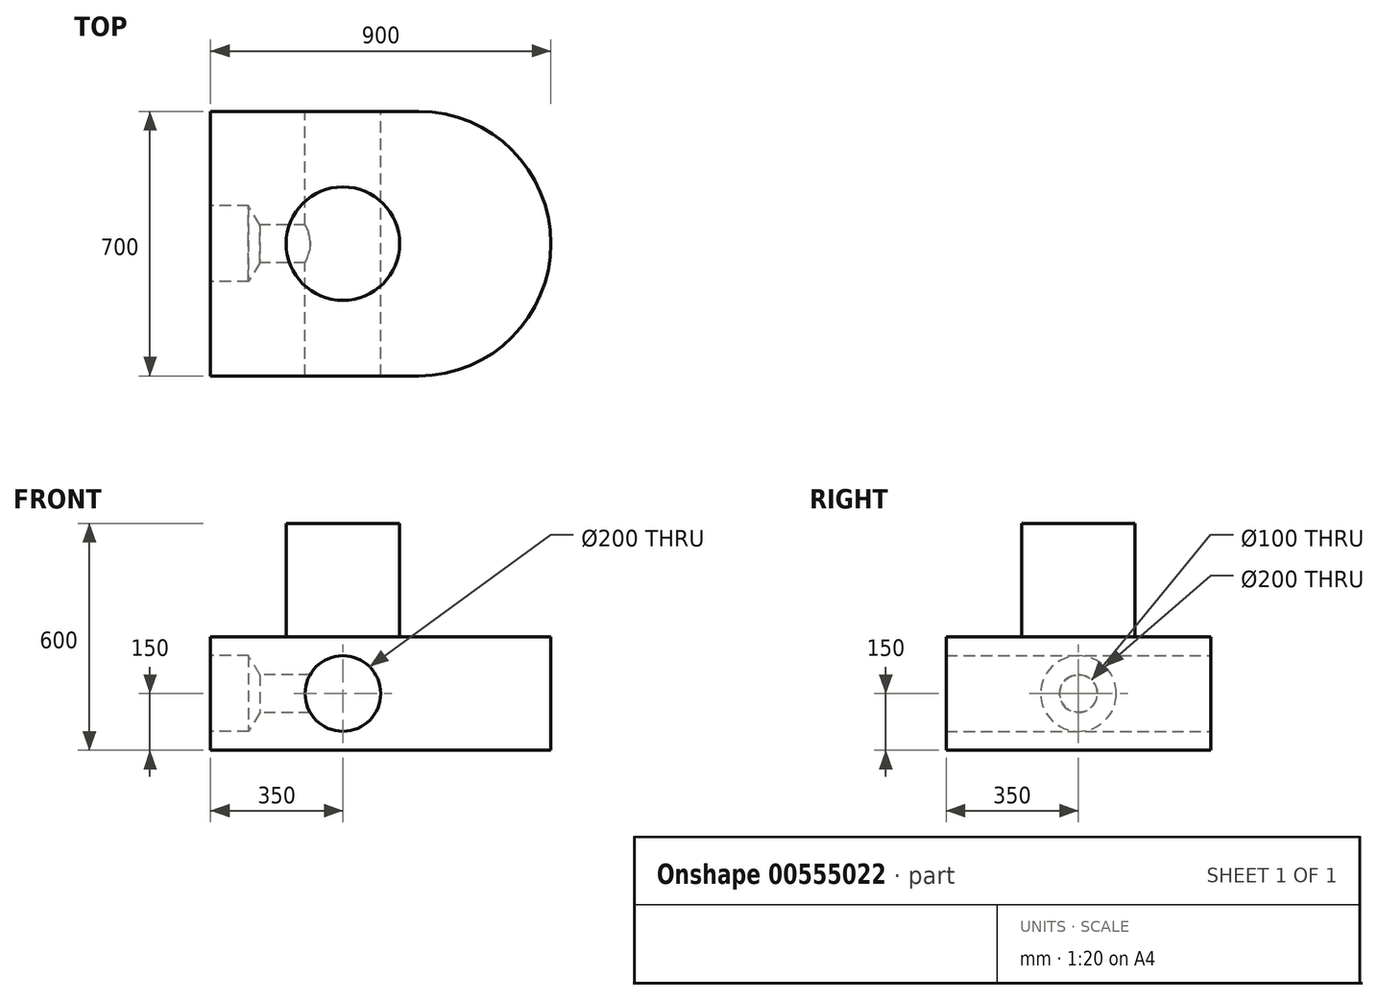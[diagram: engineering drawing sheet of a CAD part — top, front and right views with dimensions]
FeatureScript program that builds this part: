
annotation { "Feature Type Name" : "Feature", "Feature Type Description" : "" }
export const myFeature = defineFeature(function(context is Context, id is Id, definition is map)
    precondition{}
    {
        {
            var Q0;
            Q0=qCreatedBy(makeId("Front.planeOp"),FACE);
            var sketch = newSketch(context, id + "F0", { "sketchPlane" : qUnion([Q0])});
            skLineSegment(sketch, "E0", {"start": v(0, 0) * mm, "end": v(0, 300) * mm});
            skLineSegment(sketch, "E1", {"start": v(0, 300) * mm, "end": v(550, 300) * mm});
            skLineSegment(sketch, "E2", {"start": v(550, 300) * mm, "end": v(550, 0) * mm});
            skLineSegment(sketch, "E3", {"start": v(550, 0) * mm, "end": v(0, 0) * mm});
            skCircle(sketch, "E4", {"center": v(350, 150) * mm, "radius": 100 * mm});
            skLineSegment(sketch, "E5.bottom", {"start": v(550, 300) * mm, "end": v(900, 300) * mm});
            skLineSegment(sketch, "E5.top", {"start": v(550, 0) * mm, "end": v(900, 0) * mm});
            skLineSegment(sketch, "E5.right", {"start": v(900, 300) * mm, "end": v(900, 0) * mm});
            skSolve(sketch);
        }
        {
            var Q0;
            Q0=makeQuery(id+"F0.imprint","IMPRINT",FACE,{"disambiguationData":[TD([[makeQuery(id+"F0.imprint","IMPRINT",EDGE,{"derivedFrom":sQuery(id+"F0.wireOp",EDGE,"E0")}),-1.0]])]});
            extrude(context, id + "F1", {"entities" : qUnion([Q0]), "depth" : 700 * mm});
        }
        {
            var Q0;
            Q0=makeQuery(id+"F1.opExtrude","SWEPT_FACE",FACE,{"disambiguationData":[OSD([sQuery(id+"F0.wireOp",EDGE,"E2")])]});
            var sketch = newSketch(context, id + "F2", { "sketchPlane" : qUnion([Q0])});
            skLineSegment(sketch, "E6", {"start": v(-350, 300) * mm, "end": v(-350, 0) * mm});
            skSolve(sketch);
        }
        {
            var Q0;
            {var subQ0=sQuery(id+"F2.wireOp",EDGE,"E6");Q0=makeQuery(id+"F2.imprint","IMPRINT",FACE,{"disambiguationData":[TD([[makeQuery(id+"F2.imprint","IMPRINT",EDGE,{"derivedFrom":subQ0}),-1.0]])]});}
            var Q1;
            Q1=sQuery(id+"F2.wireOp",EDGE,"E6");
            revolve(context, id + "F3", {"operationType" : NewBodyOperationType.ADD, "entities" : qUnion([Q0]), "axis" : qUnion([Q1]), "revolveType" : RevolveType.ONE_DIRECTION, "oppositeDirection" : true, "angle" : 180 * degree});
        }
        {
            var Q0;
            Q0=makeQuery(id+"F1.opExtrude","SWEPT_FACE",FACE,{"disambiguationData":[OSD([sQuery(id+"F0.wireOp",EDGE,"E0")])]});
            var sketch = newSketch(context, id + "F4", { "sketchPlane" : qUnion([Q0])});
            skLineSegment(sketch, "E7", {"start": v(350, 300) * mm, "end": v(350, 0) * mm});
            skCircle(sketch, "E8", {"center": v(350, 150) * mm, "radius": 100 * mm});
            skCircle(sketch, "E9", {"center": v(350, 150) * mm, "radius": 50 * mm});
            skSolve(sketch);
        }
        {
            var Q0;
            Q0=sQuery(id+"F4.wireOp",VERTEX,"E9.center");
            var Q1;
            Q1=makeQuery(id+"F1.opExtrude","SWEPT_BODY",BODY,{"disambiguationData":[OSD([sQuery(id+"F0.wireOp",EDGE,"E0"),sQuery(id+"F0.wireOp",EDGE,"E1"),sQuery(id+"F0.wireOp",EDGE,"E3"),sQuery(id+"F0.wireOp",EDGE,"E4"),sQuery(id+"F0.wireOp",EDGE,"E2")])]});
            hole(context, id + "F5", {"style" : HoleStyle.SIMPLE, "endStyle" : HoleEndStyle.BLIND, "holeDiameter" : 100 * mm, "holeDepth" : 350 * mm, "isTappedThrough" : true, "tappedDepth" : 12.7 * mm, "tapClearance" : 3, "locations" : qUnion([Q0]), "scope" : qUnion([Q1])});
        }
        {
            var Q0;
            Q0=sQuery(id+"F4.wireOp",VERTEX,"E9.center");
            var Q1;
            Q1=makeQuery(id+"F1.opExtrude","SWEPT_BODY",BODY,{"disambiguationData":[OSD([sQuery(id+"F0.wireOp",EDGE,"E0"),sQuery(id+"F0.wireOp",EDGE,"E1"),sQuery(id+"F0.wireOp",EDGE,"E3"),sQuery(id+"F0.wireOp",EDGE,"E4"),sQuery(id+"F0.wireOp",EDGE,"E2")])]});
            hole(context, id + "F6", {"style" : HoleStyle.SIMPLE, "endStyle" : HoleEndStyle.BLIND, "holeDiameter" : 200 * mm, "holeDepth" : 100 * mm, "isTappedThrough" : true, "tappedDepth" : 12.7 * mm, "tapClearance" : 3, "locations" : qUnion([Q0]), "scope" : qUnion([Q1])});
        }
        {
            var Q0;
            {var subQ0=sQuery(id+"F0.wireOp",EDGE,"E1");Q0=makeQuery(id+"F3.boolean.opBoolean","MERGE",FACE,{"derivedFrom":[makeQuery(id+"F1.opExtrude","SWEPT_FACE",FACE,{"disambiguationData":[OSD([subQ0])]}),makeQuery(id+"F3.opRevolve","SWEPT_FACE",FACE,{"disambiguationData":[OSD([subQ0,sQuery(id+"F0.wireOp",EDGE,"E5.bottom"),sQuery(id+"F0.wireOp",EDGE,"E2")])]})]});}
            var sketch = newSketch(context, id + "F7", { "sketchPlane" : qUnion([Q0])});
            skCircle(sketch, "E10", {"center": v(350, -350) * mm, "radius": 150 * mm});
            skSolve(sketch);
        }
        {
            var Q0;
            Q0=makeQuery(id+"F7.imprint","IMPRINT",FACE,{"disambiguationData":[TD([[makeQuery(id+"F7.imprint","IMPRINT",EDGE,{"derivedFrom":sQuery(id+"F7.wireOp",EDGE,"E10")}),1.0]])]});
            extrude(context, id + "F8", {"entities" : qUnion([Q0]), "operationType" : NewBodyOperationType.ADD, "depth" : 300 * mm});
        }
    });
